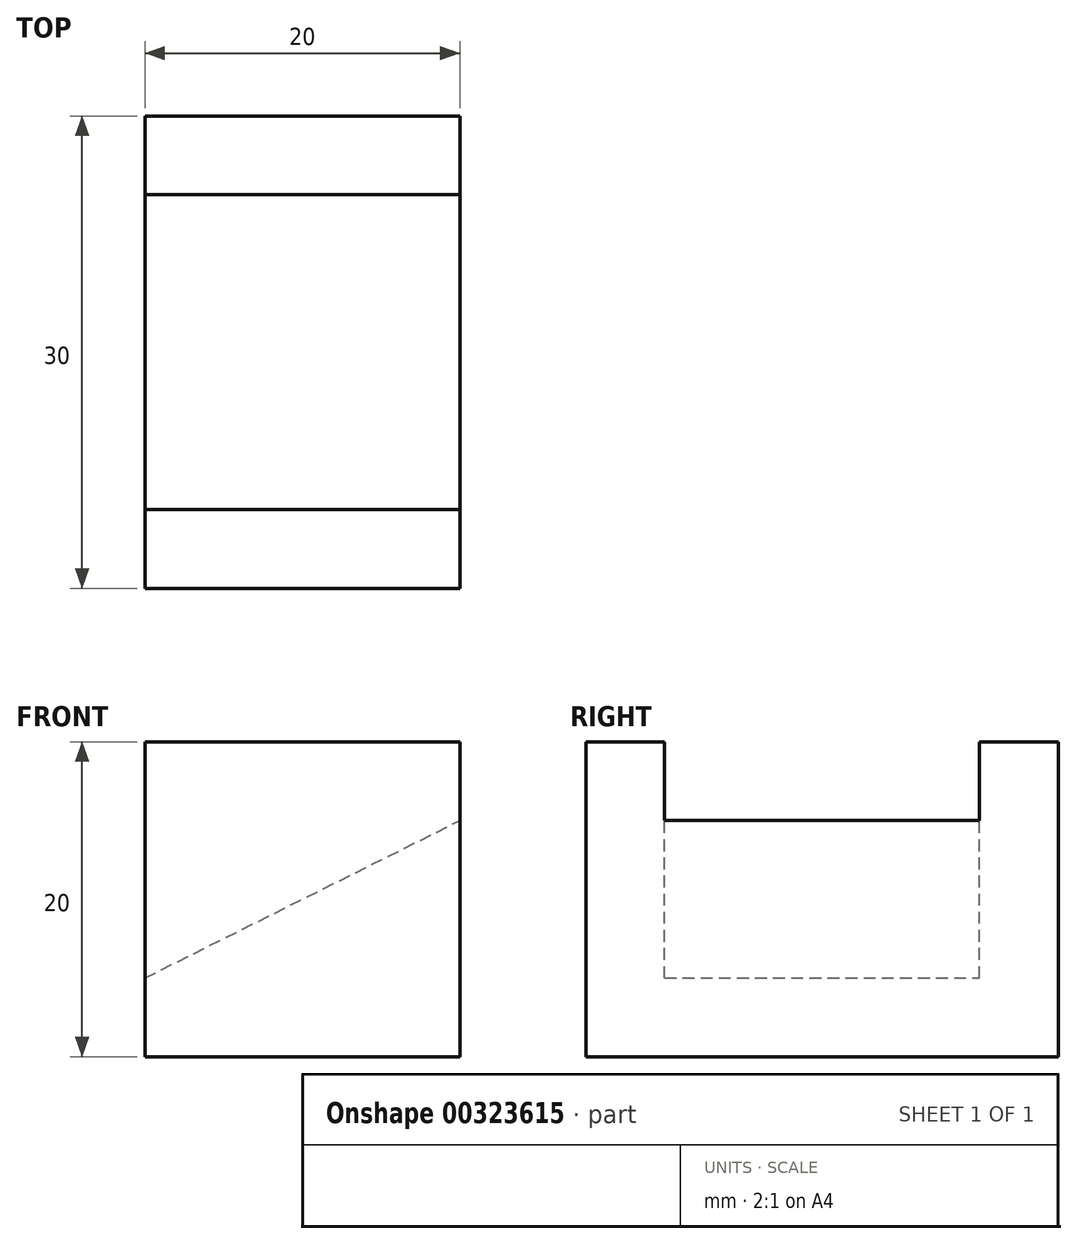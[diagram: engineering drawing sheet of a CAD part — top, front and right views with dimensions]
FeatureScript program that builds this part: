
annotation { "Feature Type Name" : "Feature", "Feature Type Description" : "" }
export const myFeature = defineFeature(function(context is Context, id is Id, definition is map)
    precondition{}
    {
        {
            var Q0;
            Q0=qCreatedBy(makeId("Front.planeOp"),FACE);
            var sketch = newSketch(context, id + "F0", { "sketchPlane" : qUnion([Q0])});
            skLineSegment(sketch, "E0", {"start": v(0, 0) * mm, "end": v(0, 20) * mm});
            skLineSegment(sketch, "E1", {"start": v(0, 20) * mm, "end": v(20, 20) * mm});
            skLineSegment(sketch, "E2", {"start": v(20, 20) * mm, "end": v(20, 0) * mm});
            skLineSegment(sketch, "E3", {"start": v(20, 0) * mm, "end": v(0, 0) * mm});
            skSolve(sketch);
        }
        {
            var Q0;
            Q0=qSketchRegion(id+"F0",true);
            extrude(context, id + "F1", {"entities" : qUnion([Q0]), "depth" : 5 * mm});
        }
        {
            var Q0;
            Q0=makeQuery(id+"F1.opExtrude","CAP_FACE",FACE,{"disambiguationData":[OSD([sQuery(id+"F0.wireOp",EDGE,"E0"),sQuery(id+"F0.wireOp",EDGE,"E1"),sQuery(id+"F0.wireOp",EDGE,"E2"),sQuery(id+"F0.wireOp",EDGE,"E3")])],"isStart":false});
            var sketch = newSketch(context, id + "F2", { "sketchPlane" : qUnion([Q0])});
            skLineSegment(sketch, "E4", {"start": v(0, 0) * mm, "end": v(0, 5) * mm});
            skLineSegment(sketch, "E5", {"start": v(0, 5) * mm, "end": v(20, 15) * mm});
            skLineSegment(sketch, "E6", {"start": v(20, 15) * mm, "end": v(20, 0) * mm});
            skLineSegment(sketch, "E7", {"start": v(20, 0) * mm, "end": v(0, 0) * mm});
            skSolve(sketch);
        }
        {
            var Q0;
            Q0=qSketchRegion(id+"F2",true);
            extrude(context, id + "F3", {"entities" : qUnion([Q0]), "operationType" : NewBodyOperationType.ADD, "depth" : 20 * mm});
        }
        {
            var Q0;
            Q0=makeQuery(id+"F3.opExtrude","CAP_FACE",FACE,{"disambiguationData":[OSD([sQuery(id+"F2.wireOp",EDGE,"E4"),sQuery(id+"F2.wireOp",EDGE,"E5"),sQuery(id+"F2.wireOp",EDGE,"E6"),sQuery(id+"F2.wireOp",EDGE,"E7")])],"isStart":false});
            var sketch = newSketch(context, id + "F4", { "sketchPlane" : qUnion([Q0])});
            skLineSegment(sketch, "E8", {"start": v(0, 0) * mm, "end": v(0, 20) * mm});
            skPoint(sketch, "E8.endSnap0", {"position": v(0, 2.5) * mm});
            skLineSegment(sketch, "E9", {"start": v(0, 20) * mm, "end": v(20, 20) * mm});
            skLineSegment(sketch, "E10", {"start": v(20, 20) * mm, "end": v(20, 0) * mm});
            skLineSegment(sketch, "E11", {"start": v(20, 0) * mm, "end": v(0, 0) * mm});
            skSolve(sketch);
        }
        {
            var Q0;
            Q0=qSketchRegion(id+"F4",true);
            extrude(context, id + "F5", {"entities" : qUnion([Q0]), "operationType" : NewBodyOperationType.ADD, "depth" : 5 * mm});
        }
    });
